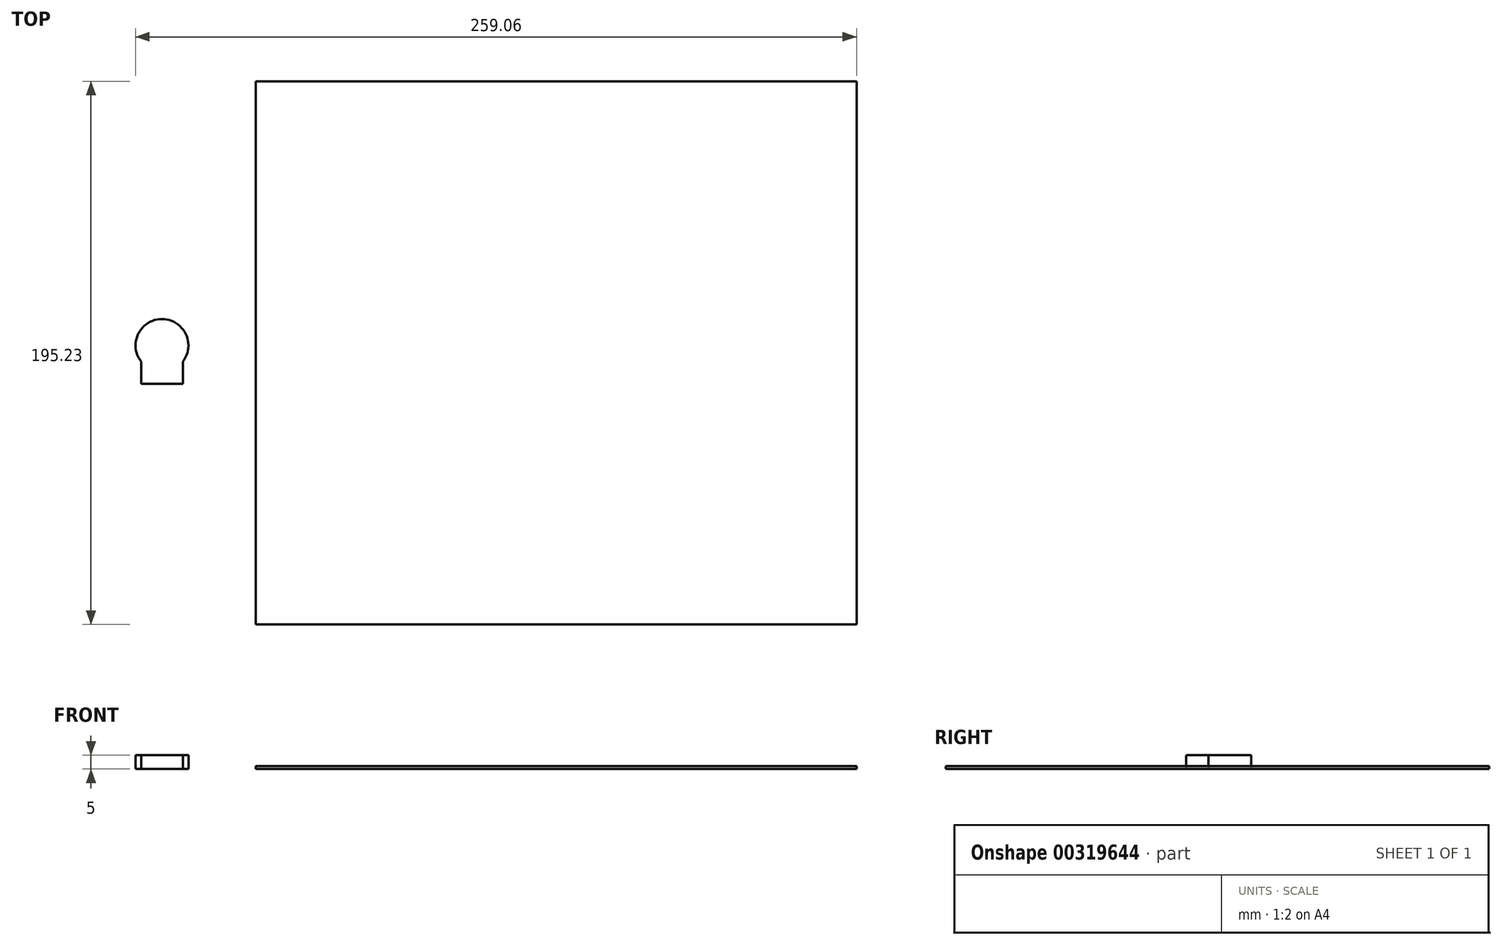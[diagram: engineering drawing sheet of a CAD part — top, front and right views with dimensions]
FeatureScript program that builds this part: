
annotation { "Feature Type Name" : "Feature", "Feature Type Description" : "" }
export const myFeature = defineFeature(function(context is Context, id is Id, definition is map)
    precondition{}
    {
        {
            var Q0;
            Q0=qCreatedBy(makeId("Top.planeOp"),FACE);
            var sketch = newSketch(context, id + "F0", { "sketchPlane" : qUnion([Q0])});
            skCircle(sketch, "E0", {"center": v(-49.05, 15.9) * mm, "radius": 9.5 * mm});
            skLineSegment(sketch, "E1.bottom", {"start": v(-56.55, 10.06) * mm, "end": v(-41.55, 10.06) * mm});
            skLineSegment(sketch, "E1.top", {"start": v(-56.55, 2.06) * mm, "end": v(-41.55, 2.06) * mm});
            skLineSegment(sketch, "E1.left", {"start": v(-56.55, 10.06) * mm, "end": v(-56.55, 2.06) * mm});
            skLineSegment(sketch, "E1.right", {"start": v(-41.55, 10.06) * mm, "end": v(-41.55, 2.06) * mm});
            skSolve(sketch);
        }
        {
            var Q0;
            Q0 = qSketchRegion(id + "F0", true);
            extrude(context, id + "F1", {"entities" : qUnion([Q0]), "depth" : 5 * mm});
        }
        {
            var Q0;
            Q0=qCreatedBy(makeId("Top.planeOp"),FACE);
            var sketch = newSketch(context, id + "F2", { "sketchPlane" : qUnion([Q0])});
            skLineSegment(sketch, "E2.bottom", {"start": v(-15.39, 110.86) * mm, "end": v(200.51, 110.86) * mm});
            skLineSegment(sketch, "E2.top", {"start": v(-15.39, -84.37) * mm, "end": v(200.51, -84.37) * mm});
            skLineSegment(sketch, "E2.left", {"start": v(-15.39, 110.86) * mm, "end": v(-15.39, -84.37) * mm});
            skLineSegment(sketch, "E2.right", {"start": v(200.51, 110.86) * mm, "end": v(200.51, -84.37) * mm});
            skSolve(sketch);
        }
        {
            var Q0;
            Q0 = qSketchRegion(id + "F2", true);
            extrude(context, id + "F3", {"entities" : qUnion([Q0]), "depth" : 1 * mm});
        }
    });
